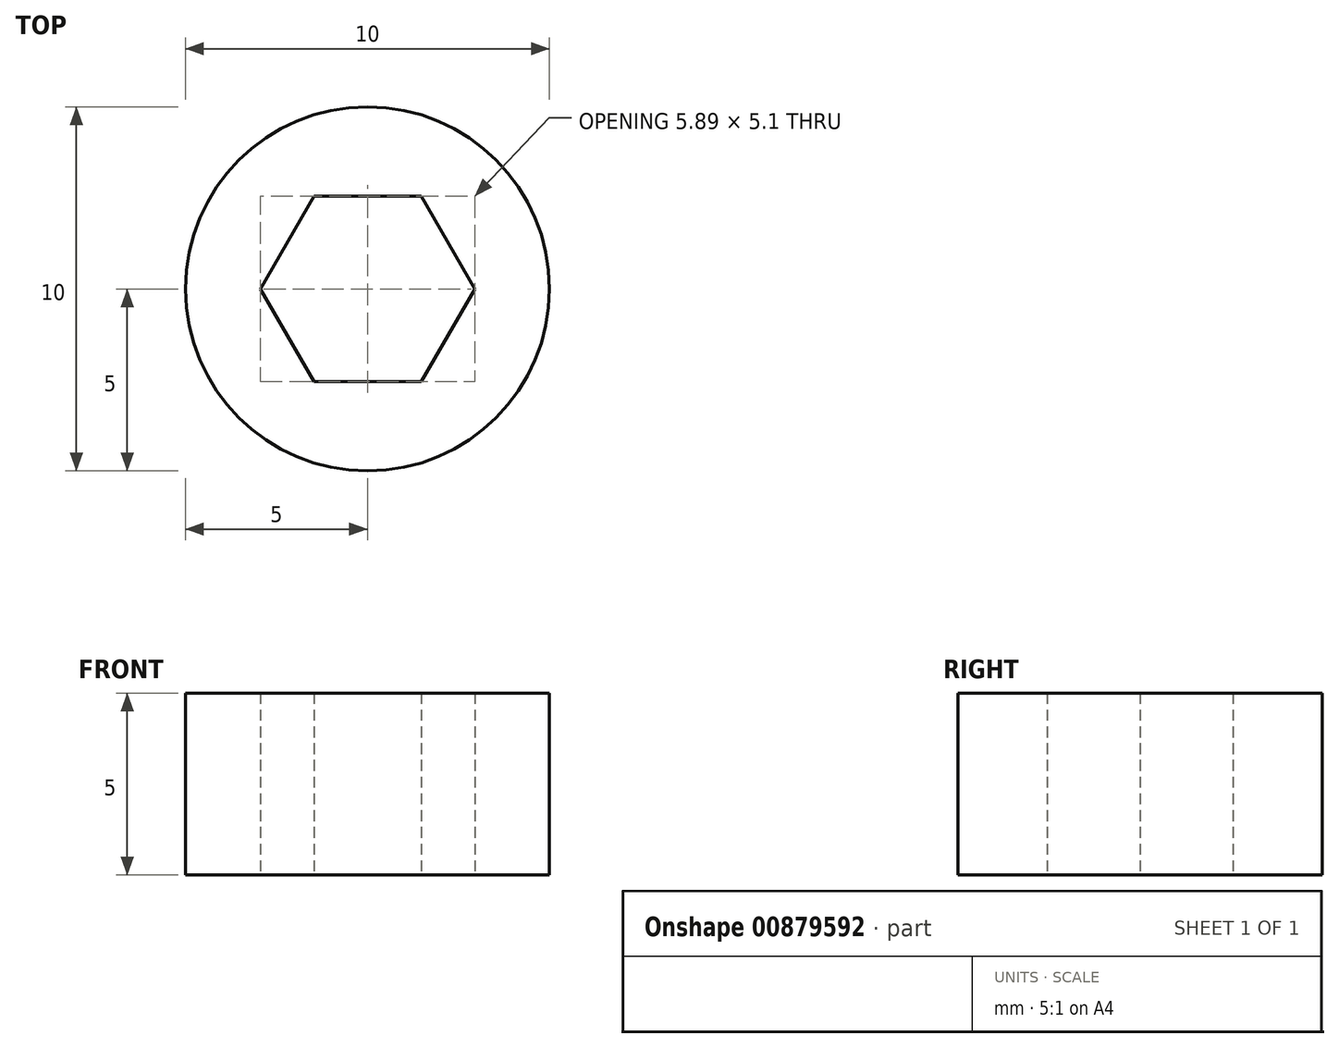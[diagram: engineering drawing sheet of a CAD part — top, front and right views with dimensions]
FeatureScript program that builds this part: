
annotation { "Feature Type Name" : "Feature", "Feature Type Description" : "" }
export const myFeature = defineFeature(function(context is Context, id is Id, definition is map)
    precondition{}
    {
        {
            assignVariable(context, id + "F0", {"name" : "thickness", "anyValue" : 5});
        }
        {
            var Q0;
            Q0=qCreatedBy(makeId("Top.planeOp"),FACE);
            var sketch = newSketch(context, id + "F1", { "sketchPlane" : qUnion([Q0])});
            skCircle(sketch, "E0.cCircle", {"center": v(0, 0) * mm, "radius": 2.55 * mm, "construction": true});
            skLineSegment(sketch, "E0.0", {"start": v(-1.47, 2.55) * mm, "end": v(1.47, 2.55) * mm});
            skLineSegment(sketch, "E0.1", {"start": v(1.47, 2.55) * mm, "end": v(2.94, 0) * mm});
            skLineSegment(sketch, "E0.2", {"start": v(2.94, 0) * mm, "end": v(1.47, -2.55) * mm});
            skLineSegment(sketch, "E0.3", {"start": v(1.47, -2.55) * mm, "end": v(-1.47, -2.55) * mm});
            skLineSegment(sketch, "E0.4", {"start": v(-1.47, -2.55) * mm, "end": v(-2.94, 0) * mm});
            skLineSegment(sketch, "E0.5", {"start": v(-2.94, 0) * mm, "end": v(-1.47, 2.55) * mm});
            skPoint(sketch, "E0.0.midPoint", {"position": v(0, 2.55) * mm});
            skCircle(sketch, "E1", {"center": v(0, 0) * mm, "radius": 5 * mm});
            skLineSegment(sketch, "E2", {"start": v(0, 2.55) * mm, "end": v(0, -2.55) * mm, "construction": true});
            skSolve(sketch);
        }
        {
            var Q0;
            Q0=makeQuery(id+"F1.imprint","IMPRINT",FACE,{"disambiguationData":[TD([[makeQuery(id+"F1.imprint","IMPRINT",EDGE,{"derivedFrom":sQuery(id+"F1.wireOp",EDGE,"E0.0")}),1.0]])]});
            extrude(context, id + "F2", {"entities" : qUnion([Q0]), "depth" : (getVariable(context, 'thickness')) * mm, "offsetDistance" : 25 * mm});
        }
    });
